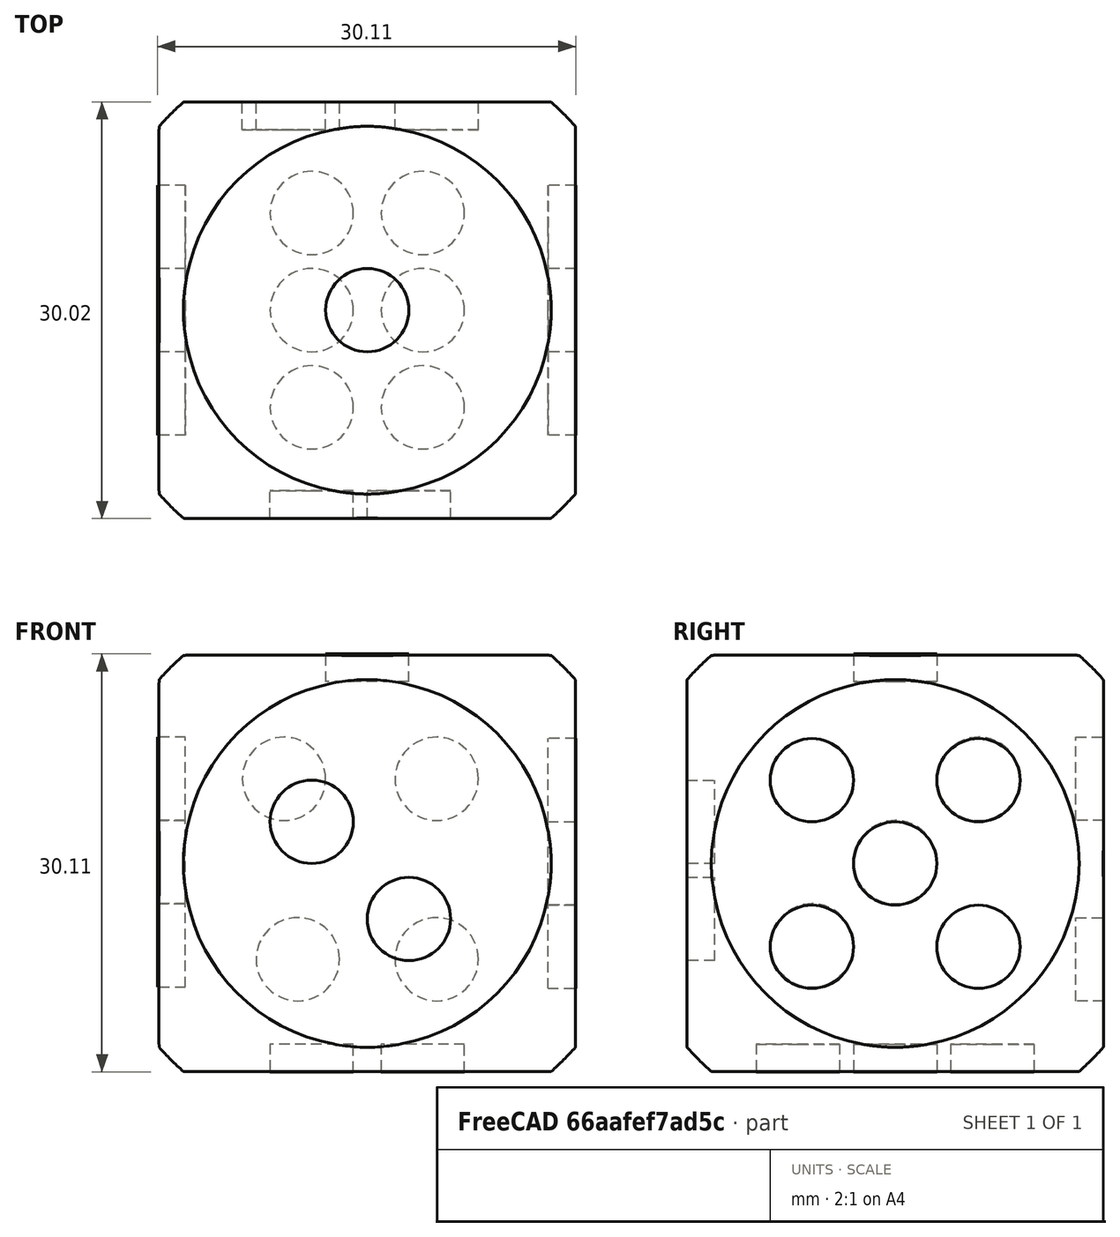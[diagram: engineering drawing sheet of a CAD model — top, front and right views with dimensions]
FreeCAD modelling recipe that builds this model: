
FCSTD DOCUMENT  (FreeCAD 0.20R29603 (Git))
Label: ielkadi_rete_2.FCStd1
License: All rights reserved
LicenseURL: http://en.wikipedia.org/wiki/All_rights_reserved
objects: Part::Cylinder×21, Part::Box×1, Part::Fillet×1, Part::Sphere×1, Part::MultiCommon×1
note: 25 computed .brp shape members not serialized (recipe doc carries the construction recipe); baked Part::Feature solids carry a one-line shape summary decoded from their .brp

FEATURE [Part::Box] Box  label="Cub"
  AttacherType = Attacher::AttachEngine3D
  Height = 30
  Length = 30
  Width = 30
FEATURE [Part::Fillet] Fillet
  Base = -> Box
  Edges = 12 edges r=2: [Edge1,Edge2,Edge3,Edge4,Edge5,Edge6,Edge7,Edge8,Edge9,Edge10,Edge11,Edge12]
FEATURE [Part::Sphere] Sphere  label="Esfera"
  Angle1 = -90
  Angle2 = 90
  Angle3 = 360
  AttacherType = Attacher::AttachEngine3D
  Placement = pos=(15,15,15) rot=(0,0,1;0rad)
  Radius = 20
FEATURE [Part::MultiCommon] Common  label="Dau"
  Shapes = -> [Fillet,Sphere]
FEATURE [Part::Cylinder] Cylinder  label="Cilindre"
  Angle = 360
  AttacherType = Attacher::AttachEngine3D
  FirstAngle = 0
  Height = 2
  Placement = pos=(-0.1,21,21.1) rot=(0,1,0;1.5708rad)
  Radius = 3
  SecondAngle = 0
FEATURE [Part::Cylinder] Cylinder001  label="Cilindre001"
  Angle = 360
  AttacherType = Attacher::AttachEngine3D
  FirstAngle = 0
  Height = 2
  Placement = pos=(19,15,-0.01) rot=(0,0,1;0rad)
  Radius = 3
  SecondAngle = 0
FEATURE [Part::Cylinder] Cylinder002  label="Cilindre002"
  Angle = 360
  AttacherType = Attacher::AttachEngine3D
  FirstAngle = 0
  Height = 2
  Placement = pos=(19,22,-0.01) rot=(0,0,1;0rad)
  Radius = 3
  SecondAngle = 0
FEATURE [Part::Cylinder] Cylinder003  label="Cilindre003"
  Angle = 360
  AttacherType = Attacher::AttachEngine3D
  FirstAngle = 0
  Height = 2
  Placement = pos=(11,22,-0.01) rot=(0,0,1;0rad)
  Radius = 3
  SecondAngle = 0
FEATURE [Part::Cylinder] Cylinder004  label="Cilindre004"
  Angle = 360
  AttacherType = Attacher::AttachEngine3D
  FirstAngle = 0
  Height = 2
  Placement = pos=(19,8,-0.01) rot=(0,0,1;0rad)
  Radius = 3
  SecondAngle = 0
FEATURE [Part::Cylinder] Cylinder007  label="Cilindre007"
  Angle = 360
  AttacherType = Attacher::AttachEngine3D
  FirstAngle = 0
  Height = 2
  Placement = pos=(11,15,-0.01) rot=(0,0,1;0rad)
  Radius = 3
  SecondAngle = 0
FEATURE [Part::Cylinder] Cylinder008  label="Cilindre008"
  Angle = 360
  AttacherType = Attacher::AttachEngine3D
  FirstAngle = 0
  Height = 2
  Placement = pos=(18,1.99,11) rot=(0.57735,0.57735,-0.57735;2.0944rad)
  Radius = 3
  SecondAngle = 0
FEATURE [Part::Cylinder] Cylinder009  label="Cilindre009"
  Angle = 360
  AttacherType = Attacher::AttachEngine3D
  FirstAngle = 0
  Height = 2
  Placement = pos=(15,15,28.1) rot=(0,0,1;0rad)
  Radius = 3
  SecondAngle = 0
FEATURE [Part::Cylinder] Cylinder010  label="Cilindre010"
  Angle = 360
  AttacherType = Attacher::AttachEngine3D
  FirstAngle = 0
  Height = 2
  Placement = pos=(9,30.01,21.1) rot=(0.57735,0.57735,-0.57735;2.0944rad)
  Radius = 3
  SecondAngle = 0
FEATURE [Part::Cylinder] Cylinder011  label="Cilindre011"
  Angle = 360
  AttacherType = Attacher::AttachEngine3D
  FirstAngle = 0
  Height = 2
  Placement = pos=(-0.1,15,15.1) rot=(0,1,0;1.5708rad)
  Radius = 3
  SecondAngle = 0
FEATURE [Part::Cylinder] Cylinder012  label="Cilindre012"
  Angle = 360
  AttacherType = Attacher::AttachEngine3D
  FirstAngle = 0
  Height = 2
  Placement = pos=(-0.1,9,9.1) rot=(0,1,0;1.5708rad)
  Radius = 3
  SecondAngle = 0
FEATURE [Part::Cylinder] Cylinder013  label="Cilindre013"
  Angle = 360
  AttacherType = Attacher::AttachEngine3D
  FirstAngle = 0
  Height = 2
  Placement = pos=(10,30.01,8.1) rot=(0.57735,0.57735,-0.57735;2.0944rad)
  Radius = 3
  SecondAngle = 0
FEATURE [Part::Cylinder] Cylinder014  label="Cilindre014"
  Angle = 360
  AttacherType = Attacher::AttachEngine3D
  FirstAngle = 0
  Height = 2
  Placement = pos=(20,30.01,8.1) rot=(0.57735,0.57735,-0.57735;2.0944rad)
  Radius = 3
  SecondAngle = 0
FEATURE [Part::Cylinder] Cylinder015  label="Cilindre015"
  Angle = 360
  AttacherType = Attacher::AttachEngine3D
  FirstAngle = 0
  Height = 2
  Placement = pos=(20,30.01,21.1) rot=(0.57735,0.57735,-0.57735;2.0944rad)
  Radius = 3
  SecondAngle = 0
FEATURE [Part::Cylinder] Cylinder016  label="Cilindre016"
  Angle = 360
  AttacherType = Attacher::AttachEngine3D
  FirstAngle = 0
  Height = 2
  Placement = pos=(11,8,-0.01) rot=(0,0,1;0rad)
  Radius = 3
  SecondAngle = 0
FEATURE [Part::Cylinder] Cylinder017  label="Cilindre017"
  Angle = 360
  AttacherType = Attacher::AttachEngine3D
  FirstAngle = 0
  Height = 2
  Placement = pos=(28.01,21,9) rot=(0,1,0;1.5708rad)
  Radius = 3
  SecondAngle = 0
FEATURE [Part::Cylinder] Cylinder018  label="Cilindre018"
  Angle = 360
  AttacherType = Attacher::AttachEngine3D
  FirstAngle = 0
  Height = 2
  Placement = pos=(11,1.99,18) rot=(0.57735,0.57735,-0.57735;2.0944rad)
  Radius = 3
  SecondAngle = 0
FEATURE [Part::Cylinder] Cylinder019  label="Cilindre019"
  Angle = 360
  AttacherType = Attacher::AttachEngine3D
  FirstAngle = 0
  Height = 2
  Placement = pos=(28.01,15,15) rot=(0,1,0;1.5708rad)
  Radius = 3
  SecondAngle = 0
FEATURE [Part::Cylinder] Cylinder020  label="Cilindre020"
  Angle = 360
  AttacherType = Attacher::AttachEngine3D
  FirstAngle = 0
  Height = 2
  Placement = pos=(28.01,21,21) rot=(0,1,0;1.5708rad)
  Radius = 3
  SecondAngle = 0
FEATURE [Part::Cylinder] Cylinder021  label="Cilindre021"
  Angle = 360
  AttacherType = Attacher::AttachEngine3D
  FirstAngle = 0
  Height = 2
  Placement = pos=(28.01,9,21) rot=(0,1,0;1.5708rad)
  Radius = 3
  SecondAngle = 0
FEATURE [Part::Cylinder] Cylinder022  label="Cilindre022"
  Angle = 360
  AttacherType = Attacher::AttachEngine3D
  FirstAngle = 0
  Height = 2
  Placement = pos=(28.01,9,9) rot=(0,1,0;1.5708rad)
  Radius = 3
  SecondAngle = 0
